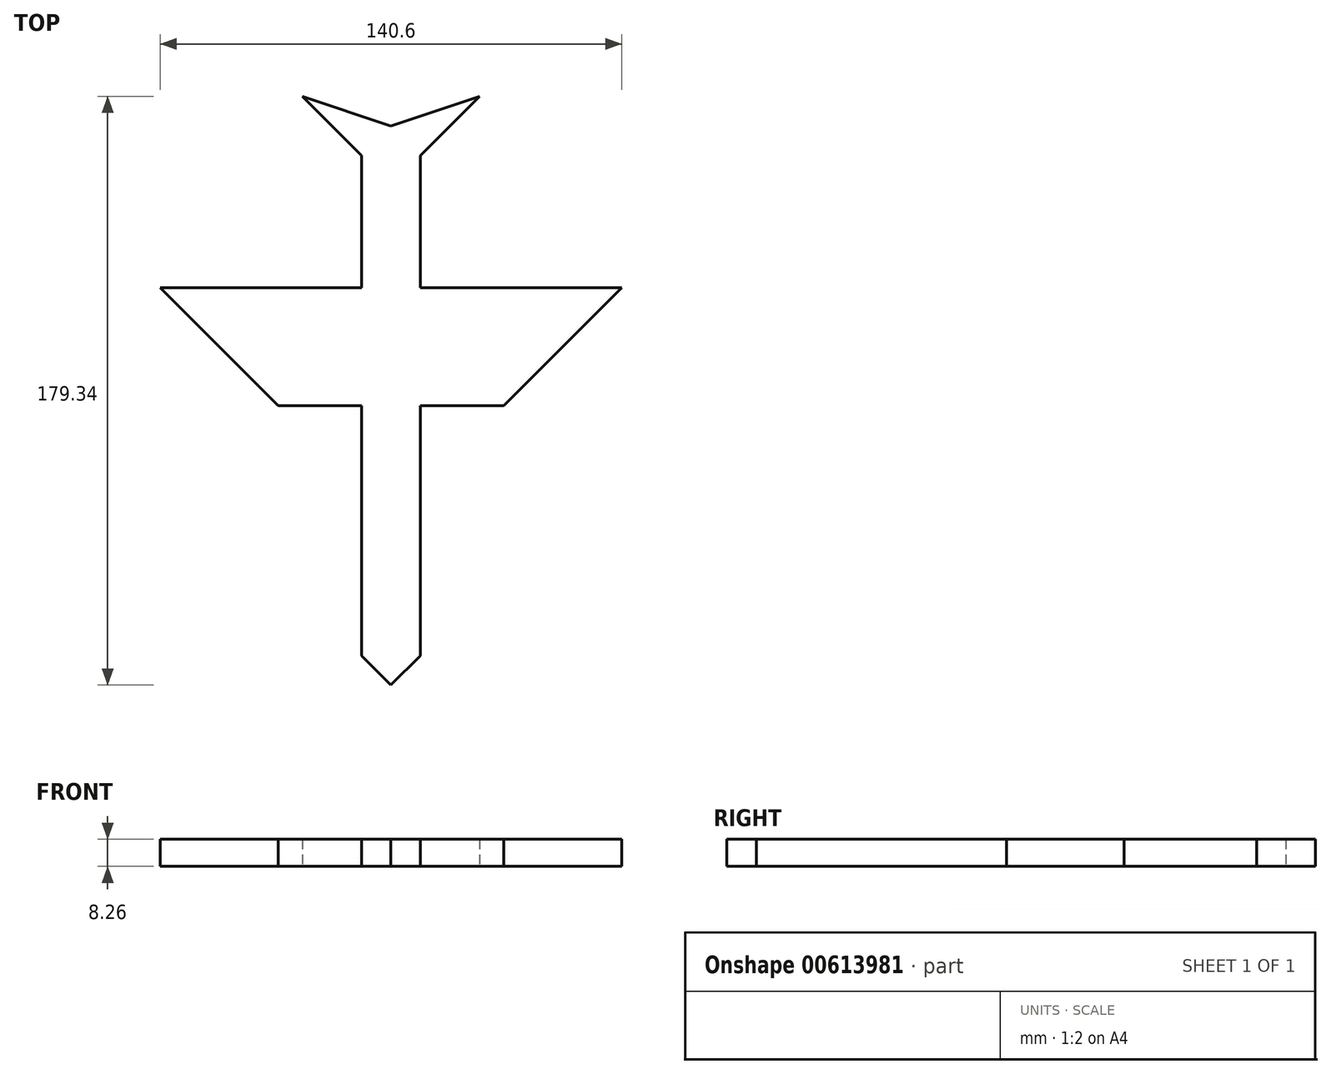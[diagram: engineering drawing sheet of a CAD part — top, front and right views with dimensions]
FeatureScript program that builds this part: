
annotation { "Feature Type Name" : "Feature", "Feature Type Description" : "" }
export const myFeature = defineFeature(function(context is Context, id is Id, definition is map)
    precondition{}
    {
        {
            var Q0;
            Q0=qCreatedBy(makeId("Top.planeOp"),FACE);
            var sketch = newSketch(context, id + "F0", { "sketchPlane" : qUnion([Q0])});
            skLineSegment(sketch, "E0", {"start": v(0, 0) * mm, "end": v(8.98, 8.98) * mm});
            skLineSegment(sketch, "E1", {"start": v(0, 0) * mm, "end": v(-8.98, 8.98) * mm});
            skLineSegment(sketch, "E2", {"start": v(8.98, 8.98) * mm, "end": v(8.98, 161.38) * mm});
            skLineSegment(sketch, "E3", {"start": v(-8.98, 8.98) * mm, "end": v(-8.98, 161.38) * mm});
            skLineSegment(sketch, "E4", {"start": v(8.98, 161.38) * mm, "end": v(8.98, 85.18) * mm});
            skLineSegment(sketch, "E5", {"start": v(-8.98, 161.38) * mm, "end": v(-8.98, 85.18) * mm});
            skLineSegment(sketch, "E6", {"start": v(-8.98, 85.18) * mm, "end": v(-34.38, 85.18) * mm});
            skLineSegment(sketch, "E7", {"start": v(-34.38, 85.18) * mm, "end": v(-70.3, 121.1) * mm});
            skLineSegment(sketch, "E8", {"start": v(-70.3, 121.1) * mm, "end": v(-8.98, 121.1) * mm});
            skLineSegment(sketch, "E9", {"start": v(8.98, 85.18) * mm, "end": v(34.38, 85.18) * mm});
            skLineSegment(sketch, "E10", {"start": v(34.38, 85.18) * mm, "end": v(70.3, 121.1) * mm});
            skLineSegment(sketch, "E11", {"start": v(70.3, 121.1) * mm, "end": v(8.98, 121.1) * mm});
            skLineSegment(sketch, "E12", {"start": v(8.98, 161.38) * mm, "end": v(-8.98, 161.38) * mm});
            skLineSegment(sketch, "E13", {"start": v(8.98, 161.38) * mm, "end": v(26.94, 179.34) * mm});
            skLineSegment(sketch, "E14", {"start": v(-8.98, 161.38) * mm, "end": v(-26.94, 179.34) * mm});
            skLineSegment(sketch, "E15", {"start": v(26.94, 179.34) * mm, "end": v(0, 170.36) * mm});
            skPoint(sketch, "E15.endSnap0", {"position": v(-17.96, 170.36) * mm});
            skLineSegment(sketch, "E16", {"start": v(0, 170.36) * mm, "end": v(-26.94, 179.34) * mm});
            skSolve(sketch);
        }
        {
            var Q0;
            Q0 = qSketchRegion(id + "F0", true);
            extrude(context, id + "F1", {"entities" : qUnion([Q0]), "depth" : 8.25 * mm, "offsetDistance" : 25.4 * mm});
        }
    });
